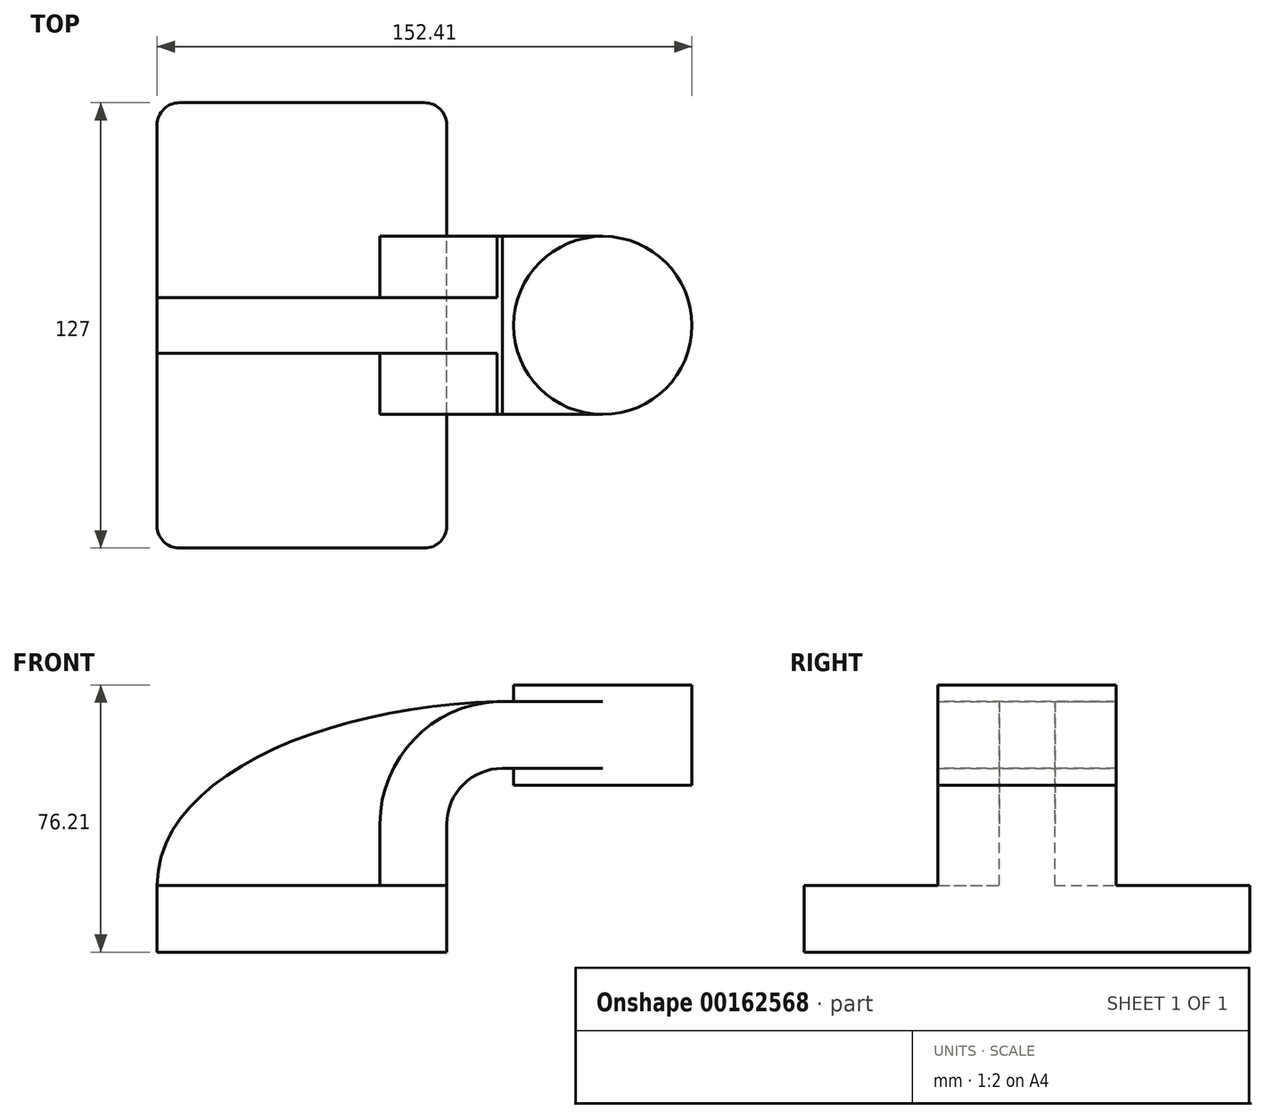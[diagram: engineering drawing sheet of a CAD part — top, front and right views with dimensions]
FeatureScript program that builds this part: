
annotation { "Feature Type Name" : "Feature", "Feature Type Description" : "" }
export const myFeature = defineFeature(function(context is Context, id is Id, definition is map)
    precondition{}
    {
        {
            var Q0;
            Q0=qCreatedBy(makeId("Front.planeOp"),FACE);
            var sketch = newSketch(context, id + "F0", { "sketchPlane" : qUnion([Q0])});
            skLineSegment(sketch, "E0.bottom", {"start": v(-41.28, -9.53) * mm, "end": v(41.28, -9.53) * mm});
            skLineSegment(sketch, "E0.top", {"start": v(-41.28, 9.52) * mm, "end": v(41.28, 9.52) * mm});
            skLineSegment(sketch, "E0.left", {"start": v(-41.28, -9.53) * mm, "end": v(-41.28, 9.52) * mm});
            skLineSegment(sketch, "E0.right", {"start": v(41.28, -9.53) * mm, "end": v(41.28, 9.52) * mm});
            skPoint(sketch, "E0.middle", {"position": v(0, 0) * mm});
            skLineSegment(sketch, "E1.bottom", {"start": v(60.32, 38.1) * mm, "end": v(111.12, 38.1) * mm});
            skLineSegment(sketch, "E1.top", {"start": v(60.32, 66.67) * mm, "end": v(111.12, 66.67) * mm});
            skLineSegment(sketch, "E1.left", {"start": v(60.32, 38.1) * mm, "end": v(60.32, 66.67) * mm});
            skLineSegment(sketch, "E1.right", {"start": v(111.12, 38.1) * mm, "end": v(111.12, 66.67) * mm});
            skPoint(sketch, "E1.middle", {"position": v(85.72, 52.39) * mm});
            skLineSegment(sketch, "E2", {"start": v(41.28, 9.52) * mm, "end": v(41.28, 27) * mm});
            skArc(sketch, "E3", {"start": v(41.27, 27) * mm, "mid": v(45.92, 38.23) * mm, "end": v(57.15, 42.88) * mm});
            skLineSegment(sketch, "E4", {"start": v(57.15, 42.88) * mm, "end": v(85.72, 42.88) * mm});
            skLineSegment(sketch, "E5.0", {"start": v(57.15, 61.93) * mm, "end": v(85.72, 61.93) * mm});
            skArc(sketch, "E5.1", {"start": v(22.22, 27) * mm, "mid": v(32.45, 51.7) * mm, "end": v(57.15, 61.93) * mm});
            skLineSegment(sketch, "E5.2", {"start": v(22.22, 9.52) * mm, "end": v(22.22, 27) * mm});
            skFitSpline(sketch, "E6", {"points": [v(-41.28, 9.53) * mm, v(57.15, 61.93) * mm], "startDerivative": vector(0.65, 97.16) * mm, "endDerivative": vector(142.22, 2.55) * mm});
            skLineSegment(sketch, "E7", {"start": v(85.72, 66.67) * mm, "end": v(85.72, 38.1) * mm});
            skSolve(sketch);
        }
        {
            var Q0;
            Q0=makeQuery(id+"F0.imprint","IMPRINT",FACE,{"disambiguationData":[TD([[makeQuery(id+"F0.imprint","IMPRINT",EDGE,{"derivedFrom":sQuery(id+"F0.wireOp",EDGE,"E0.bottom")}),1.0]])]});
            extrude(context, id + "F1", {"entities" : qUnion([Q0]), "endBound" : BoundingType.SYMMETRIC, "depth" : 127 * mm});
        }
        {
            var Q0;
            {var subQ1=sQuery(id+"F0.wireOp",EDGE,"E2");Q0=makeQuery(id+"F0.imprint","IMPRINT",FACE,{"disambiguationData":[TD([[makeQuery(id+"F0.imprint","IMPRINT",EDGE,{"derivedFrom":subQ1}),1.0]])]});}
            var Q1;
            {var subQ5=sQuery(id+"F0.wireOp",EDGE,"r2063IMt-c1Dv-mrN7-MOk0-Gl8whgYlfP9R");Q1=makeQuery(id+"F0.imprint","IMPRINT",FACE,{"disambiguationData":[TD([[makeQuery(id+"F0.imprint","IMPRINT",EDGE,{"derivedFrom":subQ5}),-1.0]])]});}
            var Q2;
            {var subQ0=sQuery(id+"F0.wireOp",EDGE,"E4");var subQ1=sQuery(id+"F0.wireOp",EDGE,"E1.left");var subQ2=makeQuery(id+"F0.imprint","INTERSECT",VERTEX,{"derivedFrom":[subQ1,subQ0]});Q2=makeQuery(id+"F0.imprint","IMPRINT",FACE,{"disambiguationData":[TD([[makeQuery(id+"F0.imprint","IMPRINT",EDGE,{"disambiguationData":[TD([[subQ2,-1.0]])],"derivedFrom":subQ1}),-1.0]])]});}
            extrude(context, id + "F2", {"entities" : qUnion([Q0, Q1, Q2]), "operationType" : NewBodyOperationType.ADD, "endBound" : BoundingType.SYMMETRIC, "depth" : 50.8 * mm});
        }
        {
            var Q0;
            {var subQ3=sQuery(id+"F0.wireOp",EDGE,"E5.2");Q0=makeQuery(id+"F0.imprint","IMPRINT",FACE,{"disambiguationData":[TD([[makeQuery(id+"F0.imprint","IMPRINT",EDGE,{"derivedFrom":subQ3}),1.0]])]});}
            extrude(context, id + "F3", {"entities" : qUnion([Q0]), "operationType" : NewBodyOperationType.ADD, "endBound" : BoundingType.SYMMETRIC, "depth" : 15.88 * mm});
        }
        {
            var Q0;
            {var subQ0=sQuery(id+"F0.wireOp",EDGE,"E1.right");Q0=makeQuery(id+"F0.imprint","IMPRINT",FACE,{"disambiguationData":[TD([[makeQuery(id+"F0.imprint","IMPRINT",EDGE,{"derivedFrom":subQ0}),1.0]])]});}
            var Q1;
            Q1=sQuery(id+"F0.wireOp",EDGE,"E7");
            revolve(context, id + "F4", {"operationType" : NewBodyOperationType.ADD, "entities" : qUnion([Q0]), "axis" : qUnion([Q1]), "revolveType" : RevolveType.FULL});
        }
        {
            var Q0;
            Q0=makeQuery(id+"F1.opExtrude","CAP_EDGE",EDGE,{"disambiguationData":[OSD([sQuery(id+"F0.wireOp",EDGE,"E0.right")])],"isStart":false});
            var Q1;
            Q1=makeQuery(id+"F1.opExtrude","CAP_EDGE",EDGE,{"disambiguationData":[OSD([sQuery(id+"F0.wireOp",EDGE,"E0.right")])],"isStart":true});
            var Q2;
            Q2=makeQuery(id+"F1.opExtrude","CAP_EDGE",EDGE,{"disambiguationData":[OSD([sQuery(id+"F0.wireOp",EDGE,"E0.left")])],"isStart":false});
            var Q3;
            Q3=makeQuery(id+"F1.opExtrude","CAP_EDGE",EDGE,{"disambiguationData":[OSD([sQuery(id+"F0.wireOp",EDGE,"E0.left")])],"isStart":true});
            fillet(context, id + "F5", {"entities" : qUnion([Q0, Q1, Q2, Q3]), "radius" : 6.35 * mm, "tangentPropagation" : true, "allowEdgeOverflow" : false});
        }
    });
